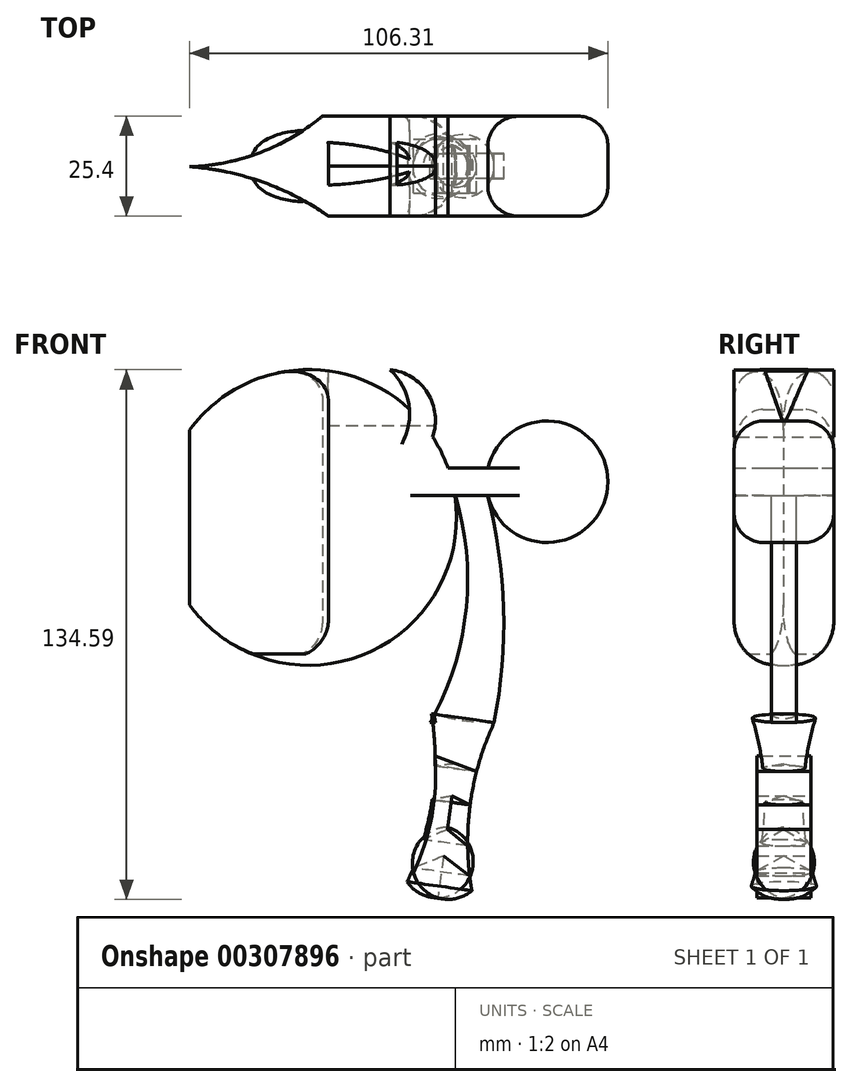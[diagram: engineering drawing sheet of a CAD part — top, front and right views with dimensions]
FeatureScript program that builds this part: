
annotation { "Feature Type Name" : "Feature", "Feature Type Description" : "" }
export const myFeature = defineFeature(function(context is Context, id is Id, definition is map)
    precondition{}
    {
        {
            var Q0;
            Q0=qCreatedBy(makeId("Front.planeOp"),FACE);
            var sketch = newSketch(context, id + "F0", { "sketchPlane" : qUnion([Q0])});
            skArc(sketch, "E0", {"start": v(-15.86, 62.15) * mm, "mid": v(-17.36, 67.63) * mm, "end": v(-20.75, 72.19) * mm});
            skArc(sketch, "E1", {"start": v(-9.97, 55.13) * mm, "mid": v(-11.24, 66.27) * mm, "end": v(-20.75, 72.19) * mm});
            skLineSegment(sketch, "E2", {"start": v(-6.05, 47.18) * mm, "end": v(4.08, 47.18) * mm});
            skLineSegment(sketch, "E3", {"start": v(4.08, 47.18) * mm, "end": v(4.08, 40.31) * mm});
            skLineSegment(sketch, "E4", {"start": v(4.08, 40.31) * mm, "end": v(-4.33, 40.31) * mm});
            skArc(sketch, "E5", {"start": v(4.08, 40.31) * mm, "mid": v(34.58, 43.75) * mm, "end": v(4.08, 47.18) * mm});
            skLineSegment(sketch, "E6", {"start": v(-15.86, 62.15) * mm, "end": v(-9.97, 55.13) * mm});
            skPoint(sketch, "E7.endSnap0", {"position": v(-0.13, 40.31) * mm});
            skCircle(sketch, "E8", {"center": v(-41.46, 34.68) * mm, "radius": 37.56 * mm});
            skSolve(sketch);
        }
        {
            var Q0;
            Q0 = qSketchRegion(id + "F0", true);
            extrude(context, id + "F1", {"entities" : qUnion([Q0]), "endBound" : BoundingType.SYMMETRIC, "depth" : 25.4 * mm});
        }
        {
            var Q0;
            Q0=qCreatedBy(makeId("Right.planeOp"),FACE);
            var sketch = newSketch(context, id + "F2", { "sketchPlane" : qUnion([Q0])});
            skLineSegment(sketch, "E9", {"start": v(-4.81, 71.89) * mm, "end": v(0, 58.05) * mm});
            skLineSegment(sketch, "E10", {"start": v(0, 58.05) * mm, "end": v(6.02, 71.89) * mm});
            skLineSegment(sketch, "E11", {"start": v(-4.81, 71.89) * mm, "end": v(6.02, 71.89) * mm});
            skSolve(sketch);
        }
        {
            var Q0;
            Q0 = qSketchRegion(id + "F2", true);
            extrude(context, id + "F3", {"entities" : qUnion([Q0]), "operationType" : NewBodyOperationType.REMOVE, "oppositeDirection" : true, "depth" : 36.58 * mm});
        }
        {
            var Q0;
            Q0=makeQuery(id+"F1.opExtrude","CAP_EDGE",EDGE,{"disambiguationData":[OSD([sQuery(id+"F0.wireOp",EDGE,"E5")])],"isStart":false});
            var Q1;
            Q1=makeQuery(id+"F1.opExtrude","CAP_EDGE",EDGE,{"disambiguationData":[OSD([sQuery(id+"F0.wireOp",EDGE,"E5")])],"isStart":true});
            fillet(context, id + "F4", {"entities" : qUnion([Q0, Q1]), "radius" : 7.62 * mm, "tangentPropagation" : true, "allowEdgeOverflow" : false});
        }
        {
            var Q0;
            Q0=qCreatedBy(makeId("Top.planeOp"),FACE);
            var sketch = newSketch(context, id + "F5", { "sketchPlane" : qUnion([Q0])});
            skArc(sketch, "E12", {"start": v(-78.1, 0) * mm, "mid": v(-42.75, 9.13) * mm, "end": v(-20.65, 38.2) * mm});
            skArc(sketch, "E13", {"start": v(-18.24, -31.58) * mm, "mid": v(-44.08, -8.03) * mm, "end": v(-78.1, 0) * mm});
            skLineSegment(sketch, "E14", {"start": v(-20.65, 38.2) * mm, "end": v(-108.18, 38.2) * mm});
            skLineSegment(sketch, "E15", {"start": v(-108.18, 38.2) * mm, "end": v(-105.17, -42.11) * mm});
            skLineSegment(sketch, "E16", {"start": v(-105.17, -42.11) * mm, "end": v(-18.24, -31.58) * mm});
            skSolve(sketch);
        }
        {
            var Q0;
            Q0 = qSketchRegion(id + "F5", true);
            extrude(context, id + "F6", {"entities" : qUnion([Q0]), "operationType" : NewBodyOperationType.REMOVE, "depth" : 77.22 * mm});
        }
        {
            var Q0;
            {var subQ0=sQuery(id+"F0.wireOp",EDGE,"E0");var subQ1=sQuery(id+"F0.wireOp",EDGE,"E8");var subQ2=sQuery(id+"F0.wireOp",EDGE,"WagRANHB-OtUp-I4nv-vQJW-JYdLZjeNDVNv");var subQ3=makeQuery(id+"F0.imprint","IMPRINT",EDGE,{"disambiguationData":[TD([[makeQuery(id+"F0.imprint","INTERSECT",VERTEX,{"derivedFrom":[subQ2,subQ1]}),1.0]])],"derivedFrom":subQ1});Q0=makeQuery(id+"F6.boolean.opBoolean","SPLIT",EDGE,{"disambiguationData":[TD([makeQuery(id+"F1.opExtrude","SWEPT_FACE",FACE,{"disambiguationData":[OSD([subQ0])]})])],"derivedFrom":makeQuery(id+"F1.opExtrude","CAP_EDGE",EDGE,{"disambiguationData":[OSD([subQ1]),TDD([subQ3])],"isStart":false})});}
            var Q1;
            {var subQ0=sQuery(id+"F0.wireOp",EDGE,"E8");var subQ1=sQuery(id+"F0.wireOp",EDGE,"WagRANHB-OtUp-I4nv-vQJW-JYdLZjeNDVNv");var subQ3=makeQuery(id+"F0.imprint","IMPRINT",EDGE,{"disambiguationData":[TD([[makeQuery(id+"F0.imprint","INTERSECT",VERTEX,{"derivedFrom":[subQ1,subQ0]}),1.0]])],"derivedFrom":subQ0});Q1=makeQuery(id+"F6.boolean.opBoolean","SPLIT",EDGE,{"disambiguationData":[TD([makeQuery(id+"F1.opExtrude","SWEPT_FACE",FACE,{"disambiguationData":[OSD([subQ1])]})])],"derivedFrom":makeQuery(id+"F1.opExtrude","CAP_EDGE",EDGE,{"disambiguationData":[OSD([subQ0]),TDD([subQ3])],"isStart":false})});}
            var Q2;
            {var subQ0=sQuery(id+"F0.wireOp",EDGE,"E0");var subQ1=sQuery(id+"F0.wireOp",EDGE,"E8");var subQ2=sQuery(id+"F0.wireOp",EDGE,"WagRANHB-OtUp-I4nv-vQJW-JYdLZjeNDVNv");var subQ3=makeQuery(id+"F0.imprint","IMPRINT",EDGE,{"disambiguationData":[TD([[makeQuery(id+"F0.imprint","INTERSECT",VERTEX,{"derivedFrom":[subQ2,subQ1]}),1.0]])],"derivedFrom":subQ1});Q2=makeQuery(id+"F6.boolean.opBoolean","SPLIT",EDGE,{"disambiguationData":[TD([makeQuery(id+"F1.opExtrude","SWEPT_FACE",FACE,{"disambiguationData":[OSD([subQ0])]})])],"derivedFrom":makeQuery(id+"F1.opExtrude","CAP_EDGE",EDGE,{"disambiguationData":[OSD([subQ1]),TDD([subQ3])],"isStart":true})});}
            var Q3;
            {var subQ0=sQuery(id+"F0.wireOp",EDGE,"E8");var subQ1=sQuery(id+"F0.wireOp",EDGE,"WagRANHB-OtUp-I4nv-vQJW-JYdLZjeNDVNv");var subQ3=makeQuery(id+"F0.imprint","IMPRINT",EDGE,{"disambiguationData":[TD([[makeQuery(id+"F0.imprint","INTERSECT",VERTEX,{"derivedFrom":[subQ1,subQ0]}),1.0]])],"derivedFrom":subQ0});Q3=makeQuery(id+"F6.boolean.opBoolean","SPLIT",EDGE,{"disambiguationData":[TD([makeQuery(id+"F1.opExtrude","SWEPT_FACE",FACE,{"disambiguationData":[OSD([subQ1])]})])],"derivedFrom":makeQuery(id+"F1.opExtrude","CAP_EDGE",EDGE,{"disambiguationData":[OSD([subQ0]),TDD([subQ3])],"isStart":true})});}
            fillet(context, id + "F7", {"entities" : qUnion([Q0, Q1, Q2, Q3]), "radius" : 7.37 * mm, "tangentPropagation" : true, "allowEdgeOverflow" : false});
        }
        {
            var Q0;
            Q0=qCreatedBy(makeId("Front.planeOp"),FACE);
            var sketch = newSketch(context, id + "F8", { "sketchPlane" : qUnion([Q0])});
            skLineSegment(sketch, "E17", {"start": v(-4.26, 40.6) * mm, "end": v(3.86, 40.6) * mm});
            skArc(sketch, "E18", {"start": v(-10.58, -17.45) * mm, "mid": v(-1.5, 10.94) * mm, "end": v(-4.26, 40.6) * mm});
            skArc(sketch, "E19", {"start": v(-14.79, -55.65) * mm, "mid": v(-9.55, -36.9) * mm, "end": v(-10.58, -17.45) * mm});
            skArc(sketch, "E20", {"start": v(-14.79, -55.65) * mm, "mid": v(-8.63, -61.96) * mm, "end": v(0, -60.16) * mm});
            skArc(sketch, "E21", {"start": v(5.67, -17.45) * mm, "mid": v(-0.45, -38.37) * mm, "end": v(0, -60.16) * mm});
            skArc(sketch, "E22", {"start": v(5.67, -17.45) * mm, "mid": v(8.04, 11.68) * mm, "end": v(3.86, 40.6) * mm});
            skLineSegment(sketch, "E23", {"start": v(-10.58, -17.45) * mm, "end": v(5.67, -17.45) * mm});
            skLineSegment(sketch, "E24", {"start": v(-9.35, -25.88) * mm, "end": v(1.21, -29.86) * mm});
            skLineSegment(sketch, "E25", {"start": v(-9.3, -33.98) * mm, "end": v(-0.45, -38.37) * mm});
            skLineSegment(sketch, "E26", {"start": v(-10.22, -41.39) * mm, "end": v(-1.06, -48.76) * mm});
            skLineSegment(sketch, "E27", {"start": v(-11.8, -47.84) * mm, "end": v(-0.56, -56.38) * mm});
            skLineSegment(sketch, "E28", {"start": v(-2.45, -17.45) * mm, "end": v(-8.63, -61.96) * mm});
            skSolve(sketch);
        }
        {
            var Q0;
            Q0=makeQuery(id+"F8.imprint","IMPRINT",FACE,{"disambiguationData":[TD([[makeQuery(id+"F8.imprint","IMPRINT",EDGE,{"derivedFrom":sQuery(id+"F8.wireOp",EDGE,"E17")}),-1.0]])]});
            extrude(context, id + "F9", {"entities" : qUnion([Q0]), "operationType" : NewBodyOperationType.ADD, "endBound" : BoundingType.SYMMETRIC, "depth" : 6.35 * mm});
        }
        {
            var Q0;
            {var subQ1=sQuery(id+"F8.wireOp",EDGE,"E21");var subQ3=sQuery(id+"F8.wireOp",EDGE,"E24");var subQ4=makeQuery(id+"F8.imprint","INTERSECT",VERTEX,{"derivedFrom":[subQ1,subQ3]});Q0=makeQuery(id+"F8.imprint","IMPRINT",FACE,{"disambiguationData":[TD([[makeQuery(id+"F8.imprint","IMPRINT",EDGE,{"disambiguationData":[TD([[subQ4,1.0]])],"derivedFrom":subQ3}),1.0]])]});}
            var Q1;
            {var subQ0=sQuery(id+"F8.wireOp",EDGE,"E25");var subQ1=sQuery(id+"F8.wireOp",EDGE,"E21");var subQ2=makeQuery(id+"F8.imprint","INTERSECT",VERTEX,{"derivedFrom":[subQ1,subQ0]});Q1=makeQuery(id+"F8.imprint","IMPRINT",FACE,{"disambiguationData":[TD([[makeQuery(id+"F8.imprint","IMPRINT",EDGE,{"disambiguationData":[TD([[subQ2,-1.0]])],"derivedFrom":subQ1}),-1.0]])]});}
            var Q2;
            {var subQ0=sQuery(id+"F8.wireOp",EDGE,"E21");var subQ1=sQuery(id+"F8.wireOp",EDGE,"E20");var subQ2=makeQuery(id+"F8.imprint","INTERSECT",VERTEX,{"derivedFrom":[subQ1,subQ0]});Q2=makeQuery(id+"F8.imprint","IMPRINT",FACE,{"disambiguationData":[TD([[makeQuery(id+"F8.imprint","IMPRINT",EDGE,{"disambiguationData":[TD([[subQ2,1.0]])],"derivedFrom":subQ1}),1.0]])]});}
            var Q3;
            Q3=sQuery(id+"F8.wireOp",EDGE,"E28");
            revolve(context, id + "F10", {"operationType" : NewBodyOperationType.ADD, "entities" : qUnion([Q0, Q1, Q2]), "axis" : qUnion([Q3]), "revolveType" : RevolveType.FULL});
        }
        {
            var Q0;
            {var subQ0=sQuery(id+"F8.wireOp",EDGE,"E24");var subQ1=sQuery(id+"F8.wireOp",EDGE,"E21");var subQ2=makeQuery(id+"F8.imprint","INTERSECT",VERTEX,{"derivedFrom":[subQ1,subQ0]});Q0=makeQuery(id+"F8.imprint","IMPRINT",FACE,{"disambiguationData":[TD([[makeQuery(id+"F8.imprint","IMPRINT",EDGE,{"disambiguationData":[TD([[subQ2,-1.0]])],"derivedFrom":subQ1}),-1.0]])]});}
            var Q1;
            {var subQ0=sQuery(id+"F8.wireOp",EDGE,"E24");var subQ1=sQuery(id+"F8.wireOp",EDGE,"E19");var subQ2=makeQuery(id+"F8.imprint","INTERSECT",VERTEX,{"derivedFrom":[subQ1,subQ0]});Q1=makeQuery(id+"F8.imprint","IMPRINT",FACE,{"disambiguationData":[TD([[makeQuery(id+"F8.imprint","IMPRINT",EDGE,{"disambiguationData":[TD([[subQ2,1.0]])],"derivedFrom":subQ1}),-1.0]])]});}
            var Q2;
            {var subQ0=sQuery(id+"F8.wireOp",EDGE,"E26");var subQ1=sQuery(id+"F8.wireOp",EDGE,"E21");var subQ2=makeQuery(id+"F8.imprint","INTERSECT",VERTEX,{"derivedFrom":[subQ1,subQ0]});Q2=makeQuery(id+"F8.imprint","IMPRINT",FACE,{"disambiguationData":[TD([[makeQuery(id+"F8.imprint","IMPRINT",EDGE,{"disambiguationData":[TD([[subQ2,-1.0]])],"derivedFrom":subQ1}),-1.0]])]});}
            var Q3;
            {var subQ0=sQuery(id+"F8.wireOp",EDGE,"E20");var subQ1=sQuery(id+"F8.wireOp",EDGE,"E19");var subQ2=makeQuery(id+"F8.imprint","INTERSECT",VERTEX,{"derivedFrom":[subQ1,subQ0]});Q3=makeQuery(id+"F8.imprint","IMPRINT",FACE,{"disambiguationData":[TD([[makeQuery(id+"F8.imprint","IMPRINT",EDGE,{"disambiguationData":[TD([[subQ2,-1.0]])],"derivedFrom":subQ1}),-1.0]])]});}
            var Q4;
            {var subQ0=sQuery(id+"F8.wireOp",EDGE,"E26");var subQ1=sQuery(id+"F8.wireOp",EDGE,"E19");var subQ2=makeQuery(id+"F8.imprint","INTERSECT",VERTEX,{"derivedFrom":[subQ1,subQ0]});Q4=makeQuery(id+"F8.imprint","IMPRINT",FACE,{"disambiguationData":[TD([[makeQuery(id+"F8.imprint","IMPRINT",EDGE,{"disambiguationData":[TD([[subQ2,1.0]])],"derivedFrom":subQ1}),-1.0]])]});}
            var Q5;
            {var subQ0=sQuery(id+"F8.wireOp",EDGE,"E25");var subQ1=sQuery(id+"F8.wireOp",EDGE,"E19");var subQ2=makeQuery(id+"F8.imprint","INTERSECT",VERTEX,{"derivedFrom":[subQ1,subQ0]});Q5=makeQuery(id+"F8.imprint","IMPRINT",FACE,{"disambiguationData":[TD([[makeQuery(id+"F8.imprint","IMPRINT",EDGE,{"disambiguationData":[TD([[subQ2,1.0]])],"derivedFrom":subQ1}),-1.0]])]});}
            extrude(context, id + "F11", {"entities" : qUnion([Q0, Q1, Q2, Q3, Q4, Q5]), "endBound" : BoundingType.SYMMETRIC, "depth" : 13.72 * mm});
        }
        {
            var Q0;
            {var subQ0=sQuery(id+"F0.wireOp",EDGE,"E8");var subQ1=sQuery(id+"F0.wireOp",EDGE,"E4");var subQ3=makeQuery(id+"F0.imprint","IMPRINT",EDGE,{"disambiguationData":[TD([[makeQuery(id+"F0.imprint","INTERSECT",VERTEX,{"derivedFrom":[subQ1,subQ0]}),1.0]])],"derivedFrom":subQ0});Q0=makeQuery(id+"F6.boolean.opBoolean","SPLIT",EDGE,{"disambiguationData":[TD([makeQuery(id+"F1.opExtrude","SWEPT_FACE",FACE,{"disambiguationData":[OSD([subQ1])]})])],"derivedFrom":makeQuery(id+"F1.opExtrude","CAP_EDGE",EDGE,{"disambiguationData":[OSD([subQ0]),TDD([subQ3])],"isStart":false})});}
            var Q1;
            {var subQ0=sQuery(id+"F0.wireOp",EDGE,"E8");var subQ1=sQuery(id+"F0.wireOp",EDGE,"E4");var subQ3=makeQuery(id+"F0.imprint","IMPRINT",EDGE,{"disambiguationData":[TD([[makeQuery(id+"F0.imprint","INTERSECT",VERTEX,{"derivedFrom":[subQ1,subQ0]}),1.0]])],"derivedFrom":subQ0});Q1=makeQuery(id+"F6.boolean.opBoolean","SPLIT",EDGE,{"disambiguationData":[TD([makeQuery(id+"F1.opExtrude","SWEPT_FACE",FACE,{"disambiguationData":[OSD([subQ1])]})])],"derivedFrom":makeQuery(id+"F1.opExtrude","CAP_EDGE",EDGE,{"disambiguationData":[OSD([subQ0]),TDD([subQ3])],"isStart":true})});}
            fillet(context, id + "F12", {"entities" : qUnion([Q0, Q1]), "radius" : 11.04 * mm, "tangentPropagation" : true, "allowEdgeOverflow" : false});
        }
    });
